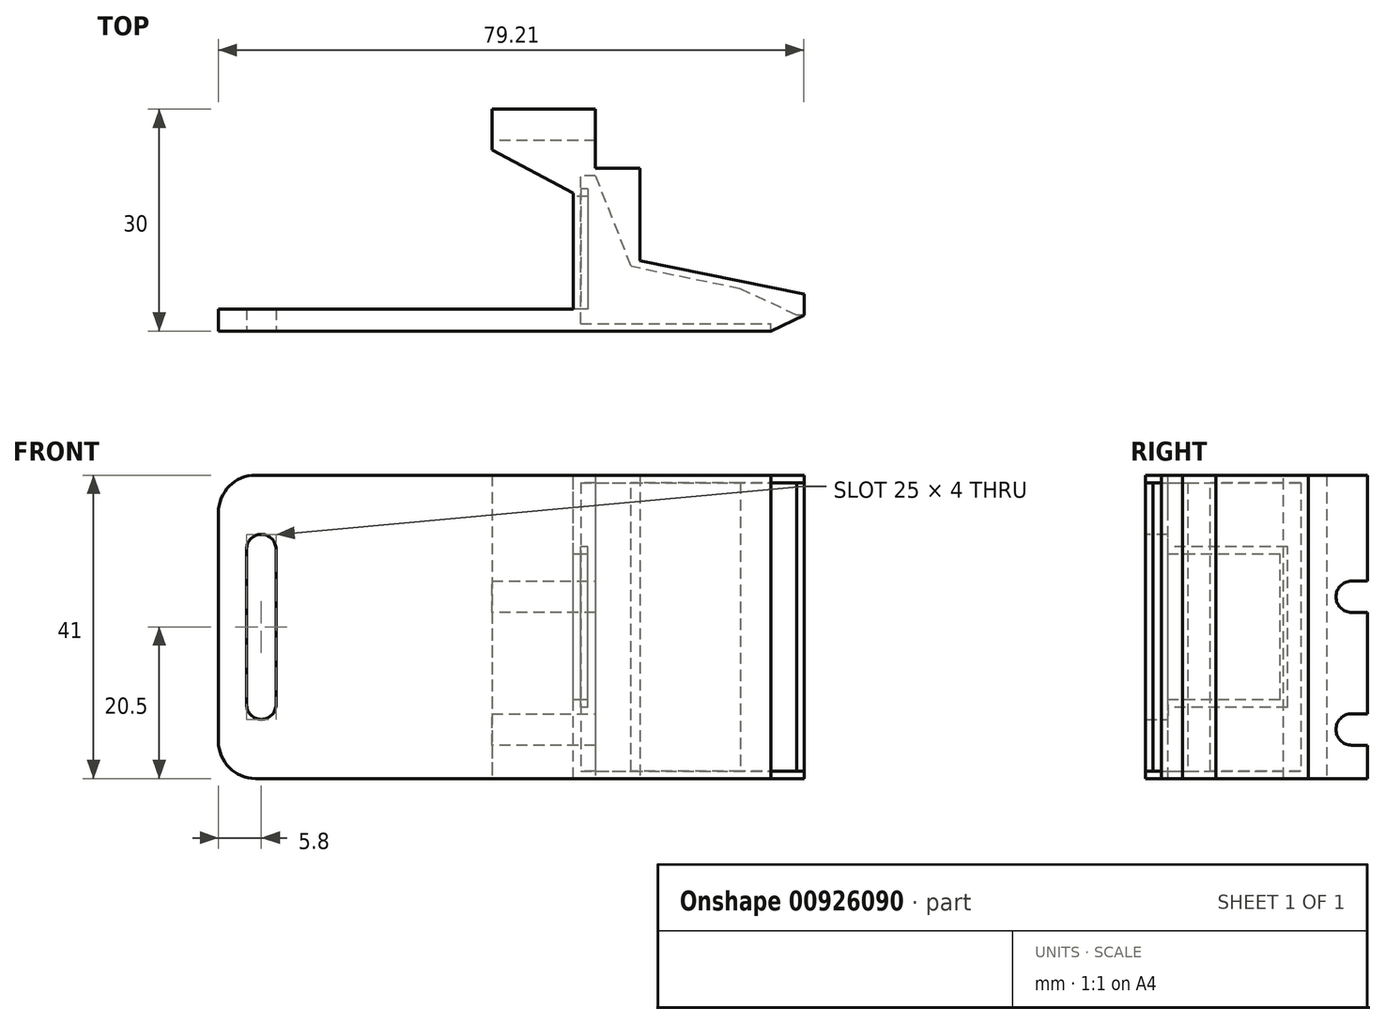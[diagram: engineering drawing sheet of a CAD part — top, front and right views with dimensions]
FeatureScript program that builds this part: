
annotation { "Feature Type Name" : "Feature", "Feature Type Description" : "" }
export const myFeature = defineFeature(function(context is Context, id is Id, definition is map)
    precondition{}
    {
        {
            var Q0;
            Q0=qCreatedBy(makeId("Top.planeOp"),FACE);
            var sketch = newSketch(context, id + "F0", { "sketchPlane" : qUnion([Q0])});
            skLineSegment(sketch, "E0", {"start": v(0, 0) * mm, "end": v(0, -8) * mm, "construction": true});
            skLineSegment(sketch, "E1", {"start": v(6, -20.5) * mm, "end": v(12, -20.5) * mm, "construction": true});
            skLineSegment(sketch, "E2", {"start": v(12, -20.5) * mm, "end": v(12, 0) * mm, "construction": true});
            skLineSegment(sketch, "E3", {"start": v(0, 0) * mm, "end": v(0, -8) * mm});
            skLineSegment(sketch, "E4", {"start": v(6, -8) * mm, "end": v(6, -20.5) * mm});
            skLineSegment(sketch, "E5", {"start": v(-3, -30) * mm, "end": v(-3, 0) * mm});
            skLineSegment(sketch, "E6", {"start": v(-3, 0) * mm, "end": v(0, 0) * mm});
            skLineSegment(sketch, "E7", {"start": v(6, -20.5) * mm, "end": v(28.21, -25) * mm});
            skLineSegment(sketch, "E8", {"start": v(-3, -30) * mm, "end": v(23.76, -30) * mm});
            skLineSegment(sketch, "E9", {"start": v(0, -8) * mm, "end": v(6, -8) * mm});
            skLineSegment(sketch, "E10.0", {"start": v(5.8, -21.48) * mm, "end": v(19.6, -24.28) * mm});
            skLineSegment(sketch, "E11.0", {"start": v(-2, -29) * mm, "end": v(23.76, -29) * mm});
            skPoint(sketch, "E12.end.orphan", {"position": v(28.21, -30) * mm});
            skLineSegment(sketch, "E13.0", {"start": v(-2, -29) * mm, "end": v(-2, -9) * mm});
            skLineSegment(sketch, "E14", {"start": v(0, -9) * mm, "end": v(-2, -9) * mm});
            skLineSegment(sketch, "E15", {"start": v(4.82, -21.28) * mm, "end": v(4.82, -21.28) * mm});
            skLineSegment(sketch, "E16", {"start": v(5.8, -21.48) * mm, "end": v(4.82, -21.28) * mm});
            skLineSegment(sketch, "E17", {"start": v(0, -9) * mm, "end": v(4.82, -21.28) * mm});
            skLineSegment(sketch, "E18", {"start": v(23.76, -30) * mm, "end": v(23.76, -29) * mm});
            skLineSegment(sketch, "E19", {"start": v(28.21, -25) * mm, "end": v(28.21, -25.9) * mm});
            skLineSegment(sketch, "E20", {"start": v(28.21, -25.9) * mm, "end": v(28.21, -27.83) * mm});
            skPoint(sketch, "E21.orphan", {"position": v(27.62, -25.9) * mm});
            skLineSegment(sketch, "E22", {"start": v(28.21, -27.83) * mm, "end": v(27.21, -27.83) * mm});
            skLineSegment(sketch, "E23", {"start": v(27.21, -27.83) * mm, "end": v(19.6, -24.28) * mm});
            skSolve(sketch);
        }
        {
            var Q0;
            Q0 = qSketchRegion(id + "F0", true);
            extrude(context, id + "F1", {"entities" : qUnion([Q0]), "depth" : 39 * mm, "offsetDistance" : 25 * mm});
        }
        {
            var Q0;
            Q0=makeQuery(id+"F1.opExtrude","CAP_FACE",FACE,{"disambiguationData":[OSD([sQuery(id+"F0.wireOp",EDGE,"E3"),sQuery(id+"F0.wireOp",EDGE,"E4"),sQuery(id+"F0.wireOp",EDGE,"E5"),sQuery(id+"F0.wireOp",EDGE,"E6"),sQuery(id+"F0.wireOp",EDGE,"E7"),sQuery(id+"F0.wireOp",EDGE,"E8"),sQuery(id+"F0.wireOp",EDGE,"E9"),sQuery(id+"F0.wireOp",EDGE,"E10.0"),sQuery(id+"F0.wireOp",EDGE,"E11.0"),sQuery(id+"F0.wireOp",EDGE,"hSjJSpao-ZVzC-N1wv-q9RY-EgTEiGcjOwMg"),sQuery(id+"F0.wireOp",EDGE,"fb6155a1-d90e-4200-b49b-709c26da296b.0"),sQuery(id+"F0.wireOp",EDGE,"7b97117f-ec5d-49e4-9a96-f440fb4eb8af.0"),sQuery(id+"F0.wireOp",EDGE,"E13.0"),sQuery(id+"F0.wireOp",EDGE,"E14"),sQuery(id+"F0.wireOp",EDGE,"E15"),sQuery(id+"F0.wireOp",EDGE,"E16"),sQuery(id+"F0.wireOp",EDGE,"3a9000da-5fcc-4d31-89f4-c9c0dca03e12.trimOffspring")])],"isStart":false});
            var sketch = newSketch(context, id + "F2", { "sketchPlane" : qUnion([Q0])});
            skLineSegment(sketch, "E24", {"start": v(-3, 0) * mm, "end": v(0, 0) * mm});
            skLineSegment(sketch, "E25", {"start": v(0, 0) * mm, "end": v(0, -8) * mm});
            skLineSegment(sketch, "E26", {"start": v(0, -8) * mm, "end": v(6, -8) * mm});
            skLineSegment(sketch, "E27", {"start": v(6, -8) * mm, "end": v(6, -20.5) * mm});
            skLineSegment(sketch, "E28", {"start": v(6, -20.5) * mm, "end": v(6, -20.5) * mm});
            skLineSegment(sketch, "E29", {"start": v(-3, -30) * mm, "end": v(-3, -30) * mm});
            skLineSegment(sketch, "E30", {"start": v(-3, -30) * mm, "end": v(-3, 0) * mm});
            skLineSegment(sketch, "E31", {"start": v(-3, -30) * mm, "end": v(23.76, -30) * mm});
            skLineSegment(sketch, "E32", {"start": v(28.21, -27.83) * mm, "end": v(28.21, -25) * mm});
            skLineSegment(sketch, "E33", {"start": v(28.21, -25) * mm, "end": v(6, -20.5) * mm});
            skLineSegment(sketch, "E34", {"start": v(23.76, -30) * mm, "end": v(28.21, -27.83) * mm});
            skPoint(sketch, "E35.orphan", {"position": v(28.21, -30) * mm});
            skSolve(sketch);
        }
        {
            var Q0;
            Q0 = qSketchRegion(id + "F2", true);
            extrude(context, id + "F3", {"entities" : qUnion([Q0]), "operationType" : NewBodyOperationType.ADD, "depth" : 1 * mm, "offsetDistance" : 25 * mm});
        }
        {
            var Q0;
            Q0=makeQuery(id+"F1.opExtrude","CAP_FACE",FACE,{"disambiguationData":[OSD([sQuery(id+"F0.wireOp",EDGE,"E3"),sQuery(id+"F0.wireOp",EDGE,"E4"),sQuery(id+"F0.wireOp",EDGE,"E5"),sQuery(id+"F0.wireOp",EDGE,"E6"),sQuery(id+"F0.wireOp",EDGE,"E7"),sQuery(id+"F0.wireOp",EDGE,"E8"),sQuery(id+"F0.wireOp",EDGE,"E9"),sQuery(id+"F0.wireOp",EDGE,"E10.0"),sQuery(id+"F0.wireOp",EDGE,"E11.0"),sQuery(id+"F0.wireOp",EDGE,"hSjJSpao-ZVzC-N1wv-q9RY-EgTEiGcjOwMg"),sQuery(id+"F0.wireOp",EDGE,"fb6155a1-d90e-4200-b49b-709c26da296b.0"),sQuery(id+"F0.wireOp",EDGE,"7b97117f-ec5d-49e4-9a96-f440fb4eb8af.0"),sQuery(id+"F0.wireOp",EDGE,"E13.0"),sQuery(id+"F0.wireOp",EDGE,"E14"),sQuery(id+"F0.wireOp",EDGE,"E15"),sQuery(id+"F0.wireOp",EDGE,"E16"),sQuery(id+"F0.wireOp",EDGE,"3a9000da-5fcc-4d31-89f4-c9c0dca03e12.trimOffspring")])],"isStart":true});
            var sketch = newSketch(context, id + "F4", { "sketchPlane" : qUnion([Q0])});
            skLineSegment(sketch, "E36", {"start": v(0, 0) * mm, "end": v(-3, 0) * mm});
            skLineSegment(sketch, "E37", {"start": v(-3, 0) * mm, "end": v(-3, 30) * mm});
            skLineSegment(sketch, "E38", {"start": v(-3, 30) * mm, "end": v(-3, 30) * mm});
            skLineSegment(sketch, "E39", {"start": v(6, 20.5) * mm, "end": v(6, 20.5) * mm});
            skLineSegment(sketch, "E40", {"start": v(6, 20.5) * mm, "end": v(6, 8) * mm});
            skLineSegment(sketch, "E41", {"start": v(6, 8) * mm, "end": v(0, 8) * mm});
            skLineSegment(sketch, "E42", {"start": v(0, 8) * mm, "end": v(0, 0) * mm});
            skLineSegment(sketch, "E43", {"start": v(-3, 30) * mm, "end": v(23.76, 30) * mm});
            skLineSegment(sketch, "E44", {"start": v(28.21, 27.83) * mm, "end": v(28.21, 25) * mm});
            skLineSegment(sketch, "E45", {"start": v(28.21, 25) * mm, "end": v(6, 20.5) * mm});
            skLineSegment(sketch, "E46", {"start": v(28.21, 27.83) * mm, "end": v(23.76, 30) * mm});
            skPoint(sketch, "E47.orphan", {"position": v(28.21, 30) * mm});
            skSolve(sketch);
        }
        {
            var Q0;
            Q0 = qSketchRegion(id + "F4", true);
            extrude(context, id + "F5", {"entities" : qUnion([Q0]), "operationType" : NewBodyOperationType.ADD, "depth" : 1 * mm, "offsetDistance" : 25 * mm});
        }
        {
            var Q0;
            Q0=makeQuery(id+"F5.boolean.opBoolean","MERGE",FACE,{"derivedFrom":[makeQuery(id+"F3.boolean.opBoolean","MERGE",FACE,{"derivedFrom":[makeQuery(id+"F1.opExtrude","SWEPT_FACE",FACE,{"disambiguationData":[OSD([sQuery(id+"F0.wireOp",EDGE,"E5")])]}),makeQuery(id+"F3.opExtrude","SWEPT_FACE",FACE,{"disambiguationData":[OSD([sQuery(id+"F2.wireOp",EDGE,"E30")])]})]}),makeQuery(id+"F5.opExtrude","SWEPT_FACE",FACE,{"disambiguationData":[OSD([sQuery(id+"F4.wireOp",EDGE,"E37")])]})]});
            var sketch = newSketch(context, id + "F6", { "sketchPlane" : qUnion([Q0])});
            skLineSegment(sketch, "E48.bottom", {"start": v(30, -1) * mm, "end": v(27, -1) * mm});
            skLineSegment(sketch, "E48.top", {"start": v(30, 40) * mm, "end": v(27, 40) * mm});
            skLineSegment(sketch, "E48.left", {"start": v(30, -1) * mm, "end": v(30, 40) * mm});
            skLineSegment(sketch, "E48.right", {"start": v(27, -1) * mm, "end": v(27, 40) * mm});
            skSolve(sketch);
        }
        {
            var Q0;
            Q0 = qSketchRegion(id + "F6", true);
            extrude(context, id + "F7", {"entities" : qUnion([Q0]), "operationType" : NewBodyOperationType.ADD, "depth" : 48 * mm, "offsetDistance" : 25 * mm});
        }
        {
            var Q0;
            Q0=makeQuery(id+"F7.boolean.opBoolean","MERGE",FACE,{"derivedFrom":[makeQuery(id+"F5.boolean.opBoolean","MERGE",FACE,{"derivedFrom":[makeQuery(id+"F3.boolean.opBoolean","MERGE",FACE,{"derivedFrom":[makeQuery(id+"F1.opExtrude","SWEPT_FACE",FACE,{"disambiguationData":[OSD([sQuery(id+"F0.wireOp",EDGE,"E8")])]}),makeQuery(id+"F3.opExtrude","SWEPT_FACE",FACE,{"disambiguationData":[OSD([sQuery(id+"F2.wireOp",EDGE,"E29")])]})]}),makeQuery(id+"F5.opExtrude","SWEPT_FACE",FACE,{"disambiguationData":[OSD([sQuery(id+"F4.wireOp",EDGE,"E38")])]})]}),makeQuery(id+"F7.opExtrude","SWEPT_FACE",FACE,{"disambiguationData":[OSD([sQuery(id+"F6.wireOp",EDGE,"E48.left")])]})]});
            var sketch = newSketch(context, id + "F8", { "sketchPlane" : qUnion([Q0])});
            skLineSegment(sketch, "E49", {"start": v(-47.2, 31.93) * mm, "end": v(-47.2, 2.4) * mm, "construction": true});
            skLineSegment(sketch, "E50", {"start": v(-51, 19.5) * mm, "end": v(-38.63, 19.5) * mm, "construction": true});
            skLineSegment(sketch, "E51.bottom", {"start": v(-47.2, 32) * mm, "end": v(-43.2, 32) * mm});
            skLineSegment(sketch, "E51.top", {"start": v(-47.2, 7) * mm, "end": v(-43.2, 7) * mm});
            skLineSegment(sketch, "E51.left", {"start": v(-47.2, 32) * mm, "end": v(-47.2, 7) * mm});
            skLineSegment(sketch, "E51.right", {"start": v(-43.2, 32) * mm, "end": v(-43.2, 7) * mm});
            skSolve(sketch);
        }
        {
            var Q0;
            Q0 = qSketchRegion(id + "F8", true);
            extrude(context, id + "F9", {"entities" : qUnion([Q0]), "operationType" : NewBodyOperationType.REMOVE, "endBound" : BoundingType.THROUGH_ALL, "oppositeDirection" : true, "depth" : 25 * mm, "offsetDistance" : 25 * mm});
        }
        {
            var Q0;
            Q0=makeQuery(id+"F9.boolean.opBoolean","COPY",EDGE,{"derivedFrom":makeQuery(id+"F9.opExtrude","SWEPT_EDGE",EDGE,{"disambiguationData":[OSD([sQuery(id+"F8.wireOp",EDGE,"E51.bottom"),sQuery(id+"F8.wireOp",EDGE,"E51.left")])]})});
            var Q1;
            Q1=makeQuery(id+"F9.boolean.opBoolean","COPY",EDGE,{"derivedFrom":makeQuery(id+"F9.opExtrude","SWEPT_EDGE",EDGE,{"disambiguationData":[OSD([sQuery(id+"F8.wireOp",EDGE,"E51.bottom"),sQuery(id+"F8.wireOp",EDGE,"E51.right")])]})});
            var Q2;
            Q2=makeQuery(id+"F9.boolean.opBoolean","COPY",EDGE,{"derivedFrom":makeQuery(id+"F9.opExtrude","SWEPT_EDGE",EDGE,{"disambiguationData":[OSD([sQuery(id+"F8.wireOp",EDGE,"E51.top"),sQuery(id+"F8.wireOp",EDGE,"E51.left")])]})});
            var Q3;
            Q3=makeQuery(id+"F9.boolean.opBoolean","COPY",EDGE,{"derivedFrom":makeQuery(id+"F9.opExtrude","SWEPT_EDGE",EDGE,{"disambiguationData":[OSD([sQuery(id+"F8.wireOp",EDGE,"E51.top"),sQuery(id+"F8.wireOp",EDGE,"E51.right")])]})});
            fillet(context, id + "F10", {"entities" : qUnion([Q0, Q1, Q2, Q3]), "radius" : 2 * mm, "tangentPropagation" : true, "allowEdgeOverflow" : false});
        }
        {
            var Q0;
            Q0=makeQuery(id+"F7.opExtrude","CAP_EDGE",EDGE,{"disambiguationData":[OSD([sQuery(id+"F6.wireOp",EDGE,"E48.top")])],"isStart":false});
            var Q1;
            Q1=makeQuery(id+"F7.opExtrude","CAP_EDGE",EDGE,{"disambiguationData":[OSD([sQuery(id+"F6.wireOp",EDGE,"E48.bottom")])],"isStart":false});
            fillet(context, id + "F11", {"entities" : qUnion([Q0, Q1]), "radius" : 5 * mm, "tangentPropagation" : true, "allowEdgeOverflow" : false});
        }
        {
            var Q0;
            Q0=makeQuery(id+"F5.boolean.opBoolean","MERGE",FACE,{"derivedFrom":[makeQuery(id+"F3.boolean.opBoolean","MERGE",FACE,{"derivedFrom":[makeQuery(id+"F1.opExtrude","SWEPT_FACE",FACE,{"disambiguationData":[OSD([sQuery(id+"F0.wireOp",EDGE,"E5")])]}),makeQuery(id+"F3.opExtrude","SWEPT_FACE",FACE,{"disambiguationData":[OSD([sQuery(id+"F2.wireOp",EDGE,"E30")])]})]}),makeQuery(id+"F5.opExtrude","SWEPT_FACE",FACE,{"disambiguationData":[OSD([sQuery(id+"F4.wireOp",EDGE,"E37")])]})]});
            var sketch = newSketch(context, id + "F12", { "sketchPlane" : qUnion([Q0])});
            skLineSegment(sketch, "E52", {"start": v(0, 19.5) * mm, "end": v(43.55, 19.5) * mm, "construction": true});
            skLineSegment(sketch, "E53.bottom", {"start": v(11.8, 9.65) * mm, "end": v(27, 9.65) * mm});
            skLineSegment(sketch, "E53.top", {"start": v(11.8, 29.35) * mm, "end": v(27, 29.35) * mm});
            skLineSegment(sketch, "E53.left", {"start": v(11.8, 9.65) * mm, "end": v(11.8, 29.35) * mm});
            skLineSegment(sketch, "E53.right", {"start": v(27, 9.65) * mm, "end": v(27, 29.35) * mm});
            skSolve(sketch);
        }
        {
            var Q0;
            Q0 = qSketchRegion(id + "F12", true);
            extrude(context, id + "F13", {"entities" : qUnion([Q0]), "operationType" : NewBodyOperationType.REMOVE, "oppositeDirection" : true, "depth" : 3 * mm, "offsetDistance" : 25 * mm});
        }
        {
            var Q0;
            Q0=makeQuery(id+"F5.boolean.opBoolean","MERGE",FACE,{"derivedFrom":[makeQuery(id+"F3.boolean.opBoolean","MERGE",FACE,{"derivedFrom":[makeQuery(id+"F1.opExtrude","SWEPT_FACE",FACE,{"disambiguationData":[OSD([sQuery(id+"F0.wireOp",EDGE,"E5")])]}),makeQuery(id+"F3.opExtrude","SWEPT_FACE",FACE,{"disambiguationData":[OSD([sQuery(id+"F2.wireOp",EDGE,"E30")])]})]}),makeQuery(id+"F5.opExtrude","SWEPT_FACE",FACE,{"disambiguationData":[OSD([sQuery(id+"F4.wireOp",EDGE,"E37")])]})]});
            var sketch = newSketch(context, id + "F14", { "sketchPlane" : qUnion([Q0])});
            skLineSegment(sketch, "E54.0", {"start": v(10.8, 8.65) * mm, "end": v(27, 8.65) * mm});
            skLineSegment(sketch, "E54.1", {"start": v(10.8, 8.65) * mm, "end": v(10.8, 30.35) * mm});
            skLineSegment(sketch, "E54.2", {"start": v(10.8, 30.35) * mm, "end": v(27, 30.35) * mm});
            skLineSegment(sketch, "E55", {"start": v(27, 8.65) * mm, "end": v(27, 9.65) * mm});
            skLineSegment(sketch, "E56", {"start": v(27, 9.65) * mm, "end": v(11.8, 9.65) * mm});
            skLineSegment(sketch, "E57", {"start": v(11.8, 9.65) * mm, "end": v(11.8, 29.35) * mm});
            skLineSegment(sketch, "E58", {"start": v(11.8, 29.35) * mm, "end": v(27, 29.35) * mm});
            skLineSegment(sketch, "E59", {"start": v(27, 29.35) * mm, "end": v(27, 30.35) * mm});
            skSolve(sketch);
        }
        {
            var Q0;
            Q0 = qSketchRegion(id + "F14", true);
            extrude(context, id + "F15", {"entities" : qUnion([Q0]), "operationType" : NewBodyOperationType.ADD, "oppositeDirection" : true, "depth" : 2 * mm, "offsetDistance" : 25 * mm});
        }
        {
            var Q0;
            Q0=makeQuery(id+"F7.boolean.opBoolean","MERGE",FACE,{"derivedFrom":[makeQuery(id+"F5.opExtrude","CAP_FACE",FACE,{"disambiguationData":[OSD([sQuery(id+"F4.wireOp",EDGE,"E36"),sQuery(id+"F4.wireOp",EDGE,"E37"),sQuery(id+"F4.wireOp",EDGE,"E40"),sQuery(id+"F4.wireOp",EDGE,"E41"),sQuery(id+"F4.wireOp",EDGE,"E42"),sQuery(id+"F4.wireOp",EDGE,"E43"),sQuery(id+"F4.wireOp",EDGE,"E44"),sQuery(id+"F4.wireOp",EDGE,"E45"),sQuery(id+"F4.wireOp",EDGE,"E46")])],"isStart":false}),makeQuery(id+"F7.opExtrude","SWEPT_FACE",FACE,{"disambiguationData":[OSD([sQuery(id+"F6.wireOp",EDGE,"E48.bottom")])]})]});
            var sketch = newSketch(context, id + "F16", { "sketchPlane" : qUnion([Q0])});
            skLineSegment(sketch, "E60", {"start": v(-3, 0) * mm, "end": v(-14, 0) * mm});
            skLineSegment(sketch, "E61", {"start": v(-14, 0) * mm, "end": v(-14, 5.5) * mm});
            skLineSegment(sketch, "E62", {"start": v(-14, 5.5) * mm, "end": v(-3, 8) * mm});
            skLineSegment(sketch, "E63", {"start": v(-3, 8) * mm, "end": v(-3, 0) * mm});
            skSolve(sketch);
        }
        {
            var Q0;
            Q0 = qSketchRegion(id + "F16", true);
            var Q1;
            Q1=makeQuery(id+"F7.boolean.opBoolean","MERGE",FACE,{"derivedFrom":[makeQuery(id+"F3.opExtrude","CAP_FACE",FACE,{"disambiguationData":[OSD([sQuery(id+"F2.wireOp",EDGE,"E24"),sQuery(id+"F2.wireOp",EDGE,"E25"),sQuery(id+"F2.wireOp",EDGE,"E26"),sQuery(id+"F2.wireOp",EDGE,"E27"),sQuery(id+"F2.wireOp",EDGE,"E30"),sQuery(id+"F2.wireOp",EDGE,"E31"),sQuery(id+"F2.wireOp",EDGE,"E32"),sQuery(id+"F2.wireOp",EDGE,"E33"),sQuery(id+"F2.wireOp",EDGE,"E34")])],"isStart":false}),makeQuery(id+"F7.opExtrude","SWEPT_FACE",FACE,{"disambiguationData":[OSD([sQuery(id+"F6.wireOp",EDGE,"E48.top")])]})]});
            extrude(context, id + "F17", {"entities" : qUnion([Q0]), "operationType" : NewBodyOperationType.ADD, "endBound" : BoundingType.UP_TO_SURFACE, "oppositeDirection" : true, "depth" : 25 * mm, "endBoundEntityFace" : qUnion([Q1]), "offsetDistance" : 25 * mm});
        }
        {
            var Q0;
            Q0=makeQuery(id+"F17.opExtrude","SWEPT_FACE",FACE,{"disambiguationData":[OSD([sQuery(id+"F16.wireOp",EDGE,"E61")])]});
            var sketch = newSketch(context, id + "F18", { "sketchPlane" : qUnion([Q0])});
            skLineSegment(sketch, "E64", {"start": v(-18.12, 3.5) * mm, "end": v(22.75, 3.5) * mm, "construction": true});
            skLineSegment(sketch, "E65", {"start": v(2.13, -5.42) * mm, "end": v(2.13, 50.83) * mm, "construction": true});
            skLineSegment(sketch, "E66", {"start": v(-6.4, 5.63) * mm, "end": v(6.18, 5.63) * mm, "construction": true});
            skArc(sketch, "E67", {"start": v(2.13, 3.5) * mm, "mid": v(4.25, 5.63) * mm, "end": v(2.13, 7.75) * mm});
            skLineSegment(sketch, "E68", {"start": v(2.13, 7.75) * mm, "end": v(-0.98, 7.75) * mm});
            skLineSegment(sketch, "E69", {"start": v(-0.98, 7.75) * mm, "end": v(-0.98, 3.5) * mm});
            skLineSegment(sketch, "E70", {"start": v(-0.98, 3.5) * mm, "end": v(2.13, 3.5) * mm});
            skLineSegment(sketch, "E71", {"start": v(-4.13, 21.45) * mm, "end": v(3.78, 21.45) * mm, "construction": true});
            skLineSegment(sketch, "E72.0", {"start": v(-4.13, 23.57) * mm, "end": v(3.78, 23.57) * mm, "construction": true});
            skArc(sketch, "E73", {"start": v(2.13, 21.45) * mm, "mid": v(4.25, 23.57) * mm, "end": v(2.13, 25.7) * mm});
            skLineSegment(sketch, "E74", {"start": v(2.13, 25.7) * mm, "end": v(-0.98, 25.7) * mm});
            skLineSegment(sketch, "E75", {"start": v(-0.98, 25.7) * mm, "end": v(-0.98, 21.45) * mm});
            skPoint(sketch, "E75.endSnap0", {"position": v(-0.17, 21.45) * mm});
            skLineSegment(sketch, "E76", {"start": v(-0.98, 21.45) * mm, "end": v(2.13, 21.45) * mm});
            skSolve(sketch);
        }
        {
            var Q0;
            Q0 = qSketchRegion(id + "F18", true);
            extrude(context, id + "F19", {"entities" : qUnion([Q0]), "operationType" : NewBodyOperationType.REMOVE, "oppositeDirection" : true, "depth" : 25 * mm, "offsetDistance" : 25 * mm});
        }
        {
            var Q0;
            Q0=makeQuery(id+"F17.boolean.opBoolean","MERGE",FACE,{"derivedFrom":[makeQuery(id+"F7.boolean.opBoolean","MERGE",FACE,{"derivedFrom":[makeQuery(id+"F3.opExtrude","CAP_FACE",FACE,{"disambiguationData":[OSD([sQuery(id+"F2.wireOp",EDGE,"E24"),sQuery(id+"F2.wireOp",EDGE,"E25"),sQuery(id+"F2.wireOp",EDGE,"E26"),sQuery(id+"F2.wireOp",EDGE,"E27"),sQuery(id+"F2.wireOp",EDGE,"E30"),sQuery(id+"F2.wireOp",EDGE,"E31"),sQuery(id+"F2.wireOp",EDGE,"E32"),sQuery(id+"F2.wireOp",EDGE,"E33"),sQuery(id+"F2.wireOp",EDGE,"E34")])],"isStart":false}),makeQuery(id+"F7.opExtrude","SWEPT_FACE",FACE,{"disambiguationData":[OSD([sQuery(id+"F6.wireOp",EDGE,"E48.top")])]})]}),makeQuery(id+"F17.opExtrude","CAP_FACE",FACE,{"disambiguationData":[OSD([sQuery(id+"F16.wireOp",EDGE,"E60"),sQuery(id+"F16.wireOp",EDGE,"E61"),sQuery(id+"F16.wireOp",EDGE,"E62"),sQuery(id+"F16.wireOp",EDGE,"E63")])],"isStart":false})]});
            var sketch = newSketch(context, id + "F20", { "sketchPlane" : qUnion([Q0])});
            skLineSegment(sketch, "E77", {"start": v(-14, -5.5) * mm, "end": v(-3, -11.35) * mm});
            skLineSegment(sketch, "E78", {"start": v(-3, -11.35) * mm, "end": v(-3, -8) * mm});
            skLineSegment(sketch, "E79", {"start": v(-3, -8) * mm, "end": v(-14, -5.5) * mm});
            skSolve(sketch);
        }
        {
            var Q0;
            Q0 = qSketchRegion(id + "F20", true);
            var Q1;
            Q1=makeQuery(id+"F17.boolean.opBoolean","MERGE",FACE,{"derivedFrom":[makeQuery(id+"F7.boolean.opBoolean","MERGE",FACE,{"derivedFrom":[makeQuery(id+"F5.opExtrude","CAP_FACE",FACE,{"disambiguationData":[OSD([sQuery(id+"F4.wireOp",EDGE,"E36"),sQuery(id+"F4.wireOp",EDGE,"E37"),sQuery(id+"F4.wireOp",EDGE,"E40"),sQuery(id+"F4.wireOp",EDGE,"E41"),sQuery(id+"F4.wireOp",EDGE,"E42"),sQuery(id+"F4.wireOp",EDGE,"E43"),sQuery(id+"F4.wireOp",EDGE,"E44"),sQuery(id+"F4.wireOp",EDGE,"E45"),sQuery(id+"F4.wireOp",EDGE,"E46")])],"isStart":false}),makeQuery(id+"F7.opExtrude","SWEPT_FACE",FACE,{"disambiguationData":[OSD([sQuery(id+"F6.wireOp",EDGE,"E48.bottom")])]})]}),makeQuery(id+"F17.opExtrude","CAP_FACE",FACE,{"disambiguationData":[OSD([sQuery(id+"F16.wireOp",EDGE,"E60"),sQuery(id+"F16.wireOp",EDGE,"E61"),sQuery(id+"F16.wireOp",EDGE,"E62"),sQuery(id+"F16.wireOp",EDGE,"E63")])],"isStart":true})]});
            extrude(context, id + "F21", {"entities" : qUnion([Q0]), "operationType" : NewBodyOperationType.ADD, "endBound" : BoundingType.UP_TO_SURFACE, "oppositeDirection" : true, "depth" : 25 * mm, "endBoundEntityFace" : qUnion([Q1]), "offsetDistance" : 25 * mm});
        }
    });
